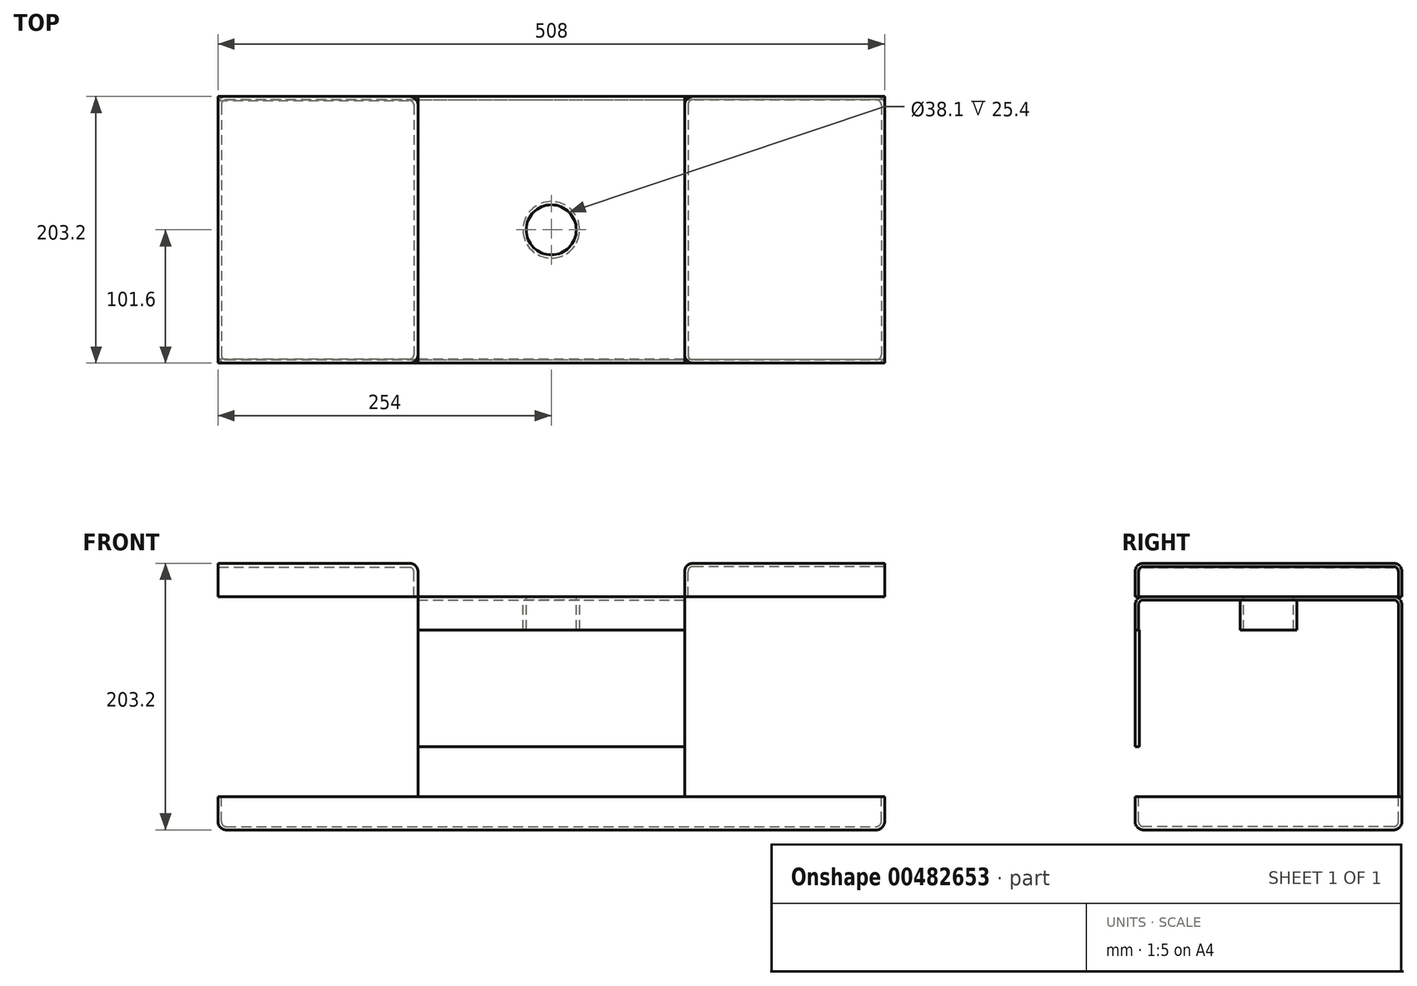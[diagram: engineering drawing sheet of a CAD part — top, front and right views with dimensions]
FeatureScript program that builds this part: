
annotation { "Feature Type Name" : "Feature", "Feature Type Description" : "" }
export const myFeature = defineFeature(function(context is Context, id is Id, definition is map)
    precondition{}
    {
        {
            var Q0;
            Q0=qCreatedBy(makeId("Right.planeOp"),FACE);
            var sketch = newSketch(context, id + "F0", { "sketchPlane" : qUnion([Q0])});
            skLineSegment(sketch, "E0", {"start": v(0, 0) * mm, "end": v(25.4, 0) * mm});
            skLineSegment(sketch, "E1", {"start": v(25.4, 0) * mm, "end": v(25.4, 152.4) * mm});
            skLineSegment(sketch, "E2", {"start": v(25.4, 152.4) * mm, "end": v(-177.8, 152.4) * mm});
            skLineSegment(sketch, "E3", {"start": v(-177.8, 152.4) * mm, "end": v(-177.8, 127) * mm});
            skLineSegment(sketch, "E4", {"start": v(-177.8, 127) * mm, "end": v(0, 127) * mm});
            skLineSegment(sketch, "E5", {"start": v(0, 127) * mm, "end": v(0, 0) * mm});
            skSolve(sketch);
        }
        {
            var Q0;
            Q0=makeQuery(id+"F0.imprint","IMPRINT",FACE,{"disambiguationData":[TD([[makeQuery(id+"F0.imprint","IMPRINT",EDGE,{"derivedFrom":sQuery(id+"F0.wireOp",EDGE,"E0")}),1.0]])]});
            extrude(context, id + "F1", {"entities" : qUnion([Q0]), "oppositeDirection" : true, "depth" : 101.6 * mm, "hasSecondDirection" : true, "secondDirectionOppositeDirection" : false, "secondDirectionDepth" : 101.6 * mm});
        }
        {
            var Q0;
            Q0=makeQuery(id+"F1.opExtrude","SWEPT_FACE",FACE,{"disambiguationData":[OSD([sQuery(id+"F0.wireOp",EDGE,"E2")])]});
            var sketch = newSketch(context, id + "F2", { "sketchPlane" : qUnion([Q0])});
            skCircle(sketch, "E6", {"center": v(0, -76.2) * mm, "radius": 19.05 * mm});
            skSolve(sketch);
        }
        {
            var Q0;
            Q0=makeQuery(id+"F2.imprint","IMPRINT",FACE,{"disambiguationData":[TD([[makeQuery(id+"F2.imprint","IMPRINT",EDGE,{"derivedFrom":sQuery(id+"F2.wireOp",EDGE,"E6")}),1.0]])]});
            extrude(context, id + "F3", {"entities" : qUnion([Q0]), "operationType" : NewBodyOperationType.REMOVE, "oppositeDirection" : true, "depth" : 25.4 * mm});
        }
        {
            var Q0;
            Q0=makeQuery(id+"F1.opExtrude","SWEPT_EDGE",EDGE,{"disambiguationData":[OSD([sQuery(id+"F0.wireOp",EDGE,"E1"),sQuery(id+"F0.wireOp",EDGE,"E2")])]});
            var Q1;
            Q1=makeQuery(id+"F1.opExtrude","SWEPT_EDGE",EDGE,{"disambiguationData":[OSD([sQuery(id+"F0.wireOp",EDGE,"E2"),sQuery(id+"F0.wireOp",EDGE,"E3")])]});
            fillet(context, id + "F4", {"entities" : qUnion([Q0, Q1]), "radius" : 6.35 * mm, "tangentPropagation" : true, "allowEdgeOverflow" : false});
        }
        {
            var Q0;
            Q0=makeQuery(id+"F1.opExtrude","CAP_FACE",FACE,{"disambiguationData":[OSD([sQuery(id+"F0.wireOp",EDGE,"E0"),sQuery(id+"F0.wireOp",EDGE,"E1"),sQuery(id+"F0.wireOp",EDGE,"E2"),sQuery(id+"F0.wireOp",EDGE,"E3"),sQuery(id+"F0.wireOp",EDGE,"E4"),sQuery(id+"F0.wireOp",EDGE,"E5")])],"isStart":false});
            var sketch = newSketch(context, id + "F5", { "sketchPlane" : qUnion([Q0])});
            skLineSegment(sketch, "E7", {"start": v(177.8, 152.4) * mm, "end": v(177.8, 177.8) * mm});
            skLineSegment(sketch, "E8", {"start": v(177.8, 177.8) * mm, "end": v(-25.4, 177.8) * mm});
            skLineSegment(sketch, "E9", {"start": v(-25.4, 177.8) * mm, "end": v(-25.4, 152.4) * mm});
            skLineSegment(sketch, "E10", {"start": v(-25.4, 152.4) * mm, "end": v(177.8, 152.4) * mm});
            skSolve(sketch);
        }
        {
            var Q0;
            {var subQ7=sQuery(id+"F5.wireOp",EDGE,"E7");Q0=makeQuery(id+"F5.imprint","IMPRINT",FACE,{"disambiguationData":[TD([[makeQuery(id+"F5.imprint","IMPRINT",EDGE,{"derivedFrom":subQ7}),1.0]])]});}
            extrude(context, id + "F6", {"entities" : qUnion([Q0]), "depth" : 152.4 * mm});
        }
        {
            var Q0;
            Q0=makeQuery(id+"F6.opExtrude","CAP_EDGE",EDGE,{"disambiguationData":[OSD([sQuery(id+"F5.wireOp",EDGE,"E9")])],"isStart":true});
            var Q1;
            Q1=makeQuery(id+"F6.opExtrude","CAP_EDGE",EDGE,{"disambiguationData":[OSD([sQuery(id+"F5.wireOp",EDGE,"E8")])],"isStart":true});
            var Q2;
            Q2=makeQuery(id+"F6.opExtrude","SWEPT_EDGE",EDGE,{"disambiguationData":[OSD([sQuery(id+"F5.wireOp",EDGE,"E8"),sQuery(id+"F5.wireOp",EDGE,"E9")])]});
            var Q3;
            Q3=makeQuery(id+"F6.opExtrude","SWEPT_EDGE",EDGE,{"disambiguationData":[OSD([sQuery(id+"F5.wireOp",EDGE,"E7"),sQuery(id+"F5.wireOp",EDGE,"E8")])]});
            var Q4;
            Q4=makeQuery(id+"F6.opExtrude","CAP_EDGE",EDGE,{"disambiguationData":[OSD([sQuery(id+"F5.wireOp",EDGE,"E7")])],"isStart":true});
            fillet(context, id + "F7", {"entities" : qUnion([Q0, Q1, Q2, Q3, Q4]), "radius" : 6.35 * mm, "tangentPropagation" : true, "allowEdgeOverflow" : false});
        }
        {
            var Q0;
            Q0=makeQuery(id+"F6.opExtrude","SWEPT_BODY",BODY,{"disambiguationData":[OSD([sQuery(id+"F5.wireOp",EDGE,"E7"),sQuery(id+"F5.wireOp",EDGE,"E8"),sQuery(id+"F5.wireOp",EDGE,"E9"),sQuery(id+"F5.wireOp",EDGE,"E10")])]});
            var Q1;
            Q1=qCreatedBy(makeId("Right.planeOp"),FACE);
            mirror(context, id + "F8", {"entities" : qUnion([Q0]), "mirrorPlane" : qUnion([Q1])});
        }
        {
            var Q0;
            Q0=makeQuery(id+"F1.opExtrude","SWEPT_FACE",FACE,{"disambiguationData":[OSD([sQuery(id+"F0.wireOp",EDGE,"E0")])]});
            var sketch = newSketch(context, id + "F9", { "sketchPlane" : qUnion([Q0])});
            skLineSegment(sketch, "E11.bottom", {"start": v(254, -25.4) * mm, "end": v(-254, -25.4) * mm});
            skLineSegment(sketch, "E11.top", {"start": v(254, 177.8) * mm, "end": v(-254, 177.8) * mm});
            skLineSegment(sketch, "E11.left", {"start": v(254, -25.4) * mm, "end": v(254, 177.8) * mm});
            skLineSegment(sketch, "E11.right", {"start": v(-254, -25.4) * mm, "end": v(-254, 177.8) * mm});
            skSolve(sketch);
        }
        {
            var Q0;
            Q0 = qSketchRegion(id + "F9", true);
            extrude(context, id + "F10", {"entities" : qUnion([Q0]), "operationType" : NewBodyOperationType.ADD, "depth" : 25.4 * mm});
        }
        {
            var Q0;
            Q0=makeQuery(id+"F10.opExtrude","SWEPT_EDGE",EDGE,{"disambiguationData":[OSD([sQuery(id+"F9.wireOp",EDGE,"E11.top"),sQuery(id+"F9.wireOp",EDGE,"E11.right")])]});
            var Q1;
            Q1=makeQuery(id+"F10.opExtrude","CAP_EDGE",EDGE,{"disambiguationData":[OSD([sQuery(id+"F9.wireOp",EDGE,"E11.top")])],"isStart":false});
            var Q2;
            Q2=makeQuery(id+"F10.opExtrude","SWEPT_EDGE",EDGE,{"disambiguationData":[OSD([sQuery(id+"F9.wireOp",EDGE,"E11.top"),sQuery(id+"F9.wireOp",EDGE,"E11.left")])]});
            var Q3;
            Q3=makeQuery(id+"F10.opExtrude","CAP_EDGE",EDGE,{"disambiguationData":[OSD([sQuery(id+"F9.wireOp",EDGE,"E11.left")])],"isStart":false});
            var Q4;
            Q4=makeQuery(id+"F10.opExtrude","SWEPT_EDGE",EDGE,{"disambiguationData":[OSD([sQuery(id+"F9.wireOp",EDGE,"E11.bottom"),sQuery(id+"F9.wireOp",EDGE,"E11.left")])]});
            var Q5;
            Q5=makeQuery(id+"F10.opExtrude","CAP_EDGE",EDGE,{"disambiguationData":[OSD([sQuery(id+"F9.wireOp",EDGE,"E11.bottom")])],"isStart":false});
            var Q6;
            Q6=makeQuery(id+"F10.opExtrude","CAP_EDGE",EDGE,{"disambiguationData":[OSD([sQuery(id+"F9.wireOp",EDGE,"E11.right")])],"isStart":false});
            var Q7;
            Q7=makeQuery(id+"F10.opExtrude","SWEPT_EDGE",EDGE,{"disambiguationData":[OSD([sQuery(id+"F9.wireOp",EDGE,"E11.bottom"),sQuery(id+"F9.wireOp",EDGE,"E11.right")])]});
            fillet(context, id + "F11", {"entities" : qUnion([Q0, Q1, Q2, Q3, Q4, Q5, Q6, Q7]), "radius" : 6.35 * mm, "tangentPropagation" : true, "allowEdgeOverflow" : false});
        }
        {
            var Q0;
            Q0=makeQuery(id+"F6.opExtrude","CAP_FACE",FACE,{"disambiguationData":[OSD([sQuery(id+"F5.wireOp",EDGE,"E7"),sQuery(id+"F5.wireOp",EDGE,"E8"),sQuery(id+"F5.wireOp",EDGE,"E9"),sQuery(id+"F5.wireOp",EDGE,"E10")])],"isStart":false});
            var Q1;
            Q1=makeQuery(id+"F6.opExtrude","SWEPT_FACE",FACE,{"disambiguationData":[OSD([sQuery(id+"F5.wireOp",EDGE,"E10")])]});
            shell(context, id + "F12", {"entities" : qUnion([Q0, Q1]), "thickness" : 3.17 * mm});
        }
        {
            var Q0;
            Q0=makeQuery(id+"F8.opPattern","COPY",FACE,{"derivedFrom":makeQuery(id+"F6.opExtrude","CAP_FACE",FACE,{"disambiguationData":[OSD([sQuery(id+"F5.wireOp",EDGE,"E7"),sQuery(id+"F5.wireOp",EDGE,"E8"),sQuery(id+"F5.wireOp",EDGE,"E9"),sQuery(id+"F5.wireOp",EDGE,"E10")])],"isStart":false}),"instanceName":"1"});
            var Q1;
            Q1=makeQuery(id+"F8.opPattern","COPY",FACE,{"derivedFrom":makeQuery(id+"F6.opExtrude","SWEPT_FACE",FACE,{"disambiguationData":[OSD([sQuery(id+"F5.wireOp",EDGE,"E10")])]}),"instanceName":"1"});
            shell(context, id + "F13", {"entities" : qUnion([Q0, Q1]), "thickness" : 2.54 * mm});
        }
        {
            var Q0;
            Q0=makeQuery(id+"F10.opExtrude","CAP_FACE",FACE,{"disambiguationData":[OSD([sQuery(id+"F9.wireOp",EDGE,"E11.bottom"),sQuery(id+"F9.wireOp",EDGE,"E11.top"),sQuery(id+"F9.wireOp",EDGE,"E11.left"),sQuery(id+"F9.wireOp",EDGE,"E11.right")])],"isStart":true});
            var Q1;
            Q1=makeQuery(id+"F1.opExtrude","SWEPT_FACE",FACE,{"disambiguationData":[OSD([sQuery(id+"F0.wireOp",EDGE,"E5")])]});
            var Q2;
            Q2=makeQuery(id+"F1.opExtrude","SWEPT_FACE",FACE,{"disambiguationData":[OSD([sQuery(id+"F0.wireOp",EDGE,"E4")])]});
            var Q3;
            Q3=makeQuery(id+"F1.opExtrude","CAP_FACE",FACE,{"disambiguationData":[OSD([sQuery(id+"F0.wireOp",EDGE,"E0"),sQuery(id+"F0.wireOp",EDGE,"E1"),sQuery(id+"F0.wireOp",EDGE,"E2"),sQuery(id+"F0.wireOp",EDGE,"E3"),sQuery(id+"F0.wireOp",EDGE,"E4"),sQuery(id+"F0.wireOp",EDGE,"E5")])],"isStart":false});
            var Q4;
            Q4=makeQuery(id+"F1.opExtrude","CAP_FACE",FACE,{"disambiguationData":[OSD([sQuery(id+"F0.wireOp",EDGE,"E0"),sQuery(id+"F0.wireOp",EDGE,"E1"),sQuery(id+"F0.wireOp",EDGE,"E2"),sQuery(id+"F0.wireOp",EDGE,"E3"),sQuery(id+"F0.wireOp",EDGE,"E4"),sQuery(id+"F0.wireOp",EDGE,"E5")])],"isStart":true});
            shell(context, id + "F14", {"entities" : qUnion([Q0, Q1, Q2, Q3, Q4]), "thickness" : 2.54 * mm});
        }
        {
            var Q0;
            Q0=makeQuery(id+"F1.opExtrude","SWEPT_FACE",FACE,{"disambiguationData":[OSD([sQuery(id+"F0.wireOp",EDGE,"E3")])]});
            var sketch = newSketch(context, id + "F15", { "sketchPlane" : qUnion([Q0])});
            skLineSegment(sketch, "E12.bottom", {"start": v(-101.6, 127) * mm, "end": v(101.6, 127) * mm});
            skLineSegment(sketch, "E12.top", {"start": v(-101.6, 38.1) * mm, "end": v(101.6, 38.1) * mm});
            skLineSegment(sketch, "E12.left", {"start": v(-101.6, 127) * mm, "end": v(-101.6, 38.1) * mm});
            skLineSegment(sketch, "E12.right", {"start": v(101.6, 127) * mm, "end": v(101.6, 38.1) * mm});
            skSolve(sketch);
        }
        {
            var Q0;
            Q0 = qSketchRegion(id + "F15", true);
            extrude(context, id + "F16", {"entities" : qUnion([Q0]), "oppositeDirection" : true, "depth" : 3.17 * mm});
        }
    });
